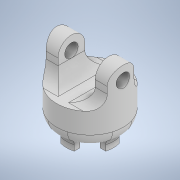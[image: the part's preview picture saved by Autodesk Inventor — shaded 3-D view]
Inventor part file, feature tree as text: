
AUTODESK INVENTOR PART (.ipt)
format: ipt  version: 2022 (Build 260153000, 153)  size: 264,704 bytes
history: native  units: in
note: dims shown in document units (in); Inventor stores cm internally (conversion verified against a paired STEP export)
features: extrude x5, sketch x5, fillet x5
ambient origin geometry x8: Origin, YZ Plane, XZ Plane, XY Plane, X Axis, Y Axis, Z Axis, Center Point
bodies: Solid1 (feature_tree)
feature tree (15):
  extrude  "Extrusion1"  Depth=0.3937in TaperAngle=0.0deg
  sketch  "Sketch2"  dims[d3=0.2756in d4=0.0787in]
  extrude  "Extrusion3"  Depth=0.0787in
  extrude  "Extrusion4"  Depth=0.0787in
  fillet  "Fillet1"  Radius=0.0787in
  fillet  "Fillet2"  Radius=0.0787in
  extrude  "Extrusion5"  Depth=0.0394in
  fillet  "Fillet3"  Radius=0.0787in
  fillet  "Fillet4"  Radius=0.0394in
  fillet  "Fillet5"  Radius=0.1181in
  extrude  "Extrusion6"  Depth=0.0394in
  sketch  "Sketch1"  dims[d0=0.3937in d1=0.1969in d2=0.0in]
  sketch  "Sketch3"  dims[d5=0.0787in d6=0.0787in d7=0.0787in d8=0.0787in]
  sketch  "Sketch4"  dims[d9=0.0787in d10=0.0787in d11=0.0787in d14=0.0394in d15=0.0in d16=0.1181in d17=0.0in]
  sketch  "Sketch5"  dims[d18=0.0787in d19=0.0394in d21=0.7874in d23=360.0deg d25=0.1969in d26=0.0in d27=0.0787in d28=0.0787in d31=0.1969in d32=0.0709in d33=0.0709in d34=0.0in d35=0.0787in d36=0.0787in d37=0.0394in d38=0.0787in d39=0.7874in d40=0.0in]
